# Revit family: Control_Unit-Lutron-Power_Over_Ethernet-Q-POE-8
name_source: partatom
category: Lighting Devices
revit_build: Autodesk Revit 2018 (Build: 20190510_1515(x64)
units: mm (PartAtom-declared; Revit-internal decimal feet)

## family parameters
Cut with Voids When Loaded = Yes
Host = Face
Maintain Annotation Orientation = Yes
OmniClass Number = 23.85.80.11
OmniClass Title = Building Controls
Part Type = Normal
Room Calculation Point = No
Round Connector Dimension = Use Radius
Shared = No

## types (1)
- Q-POE-8
    Apparent Power = 0 VA
    Assembly Code = D5020200
    Cost = 0 $
    Current = 0 A
    Default Elevation = 4' - 0"
    Description = 8 Port Power Over Ethernet Switch
    Finish = Plastic - Lutron - White - Matte
    Instruction Sheet Link = https://www.lutron.com
    Load Classification = Other
    Manufacturer = Lutron Electronics Co., Inc
    Manufacturer Fax Number = 610-282-1243
    Maximum Operating Temperature = 104 °F
    Minimum Operating Temperature = 32 °F
    Model = Q-POE-8
    Number of Poles = 1
    Operating Voltage = Input: 24 V- | Ethernet output: 48 V to 57 V-, 60 W total, 30 W max per output
    Overall Depth = 0' - 1 5/8"
    Overall Height = 0' - 6 3/16"
    Overall Width = 0' - 3 3/4"
    Performance URL = http://www.lutron.com
    Plug Bottom Edge = 0' - 0 15/16"
    Plug Height = 0' - 0 1/2"
    Plug Left Edge = 0' - 1 11/32"
    Plug Right Edge = 0' - 1 7/32"
    Plug Top Edge = 0' - 0 3/32"
    Ports Bottom Edge = 0' - 0 5/8"
    Ports Left Edge = 0' - 0 3/16"
    Ports Length = 0' - 4 7/8"
    Ports Top Edge = 0' - 0 7/16"
    Product Documentation Link = https://www.lutron.com
    Product Name = Power Over Ethernet Switch
    Product Page URL = https://www.lutron.com
    Series = Athena
    URL = http://www.lutron.com
    Version = 2018 - v1.0a
    Video Link = https://www.youtube.com
    Void Depth = 0' - 0 1/16"
    Void Inset = 0' - 0 3/32"
    Voltage = 24 V
    Warranty URL = http://www.lutron.com

## geometry (parser evidence)
native form markers: Sweep x2
no freeform markers — native parametric forms only
